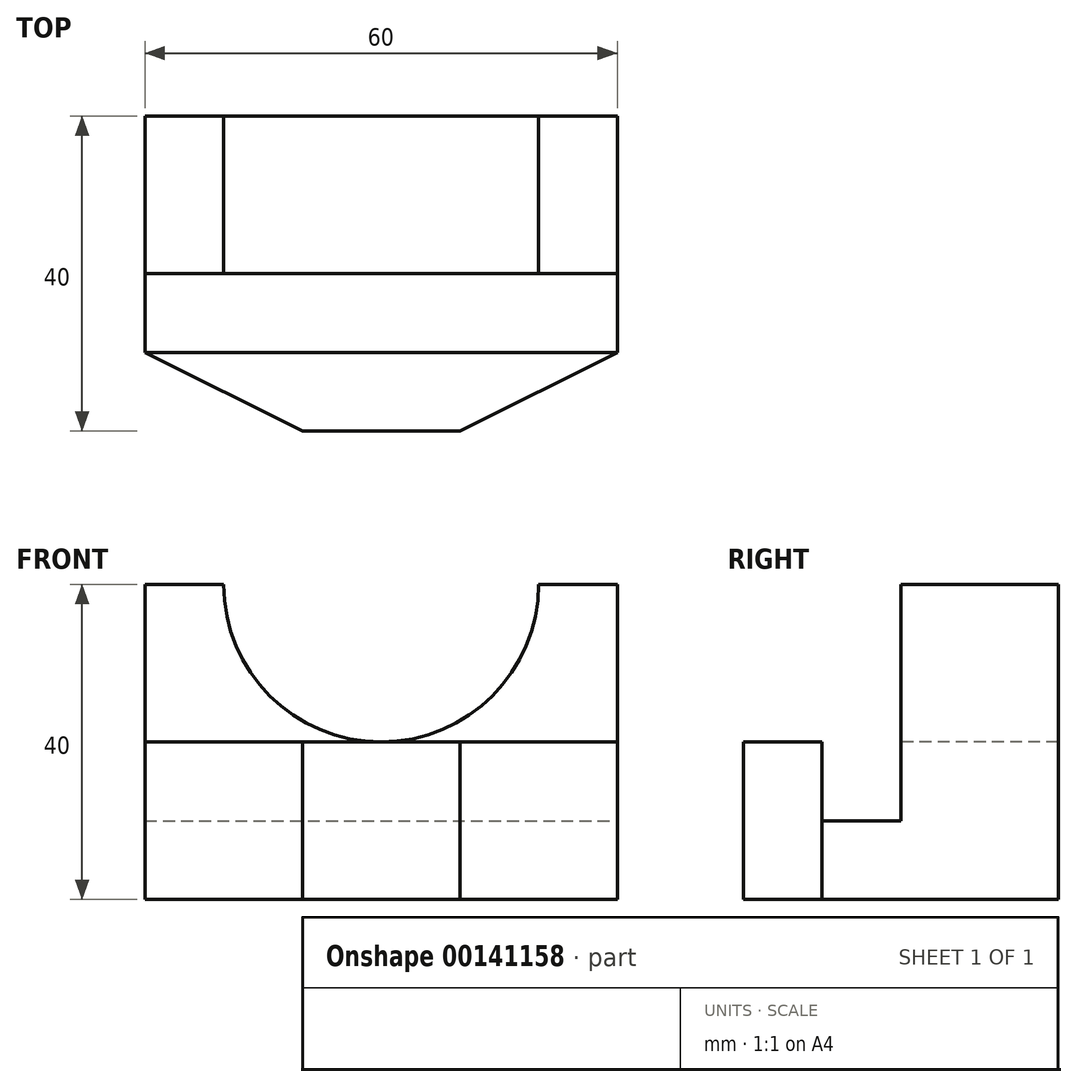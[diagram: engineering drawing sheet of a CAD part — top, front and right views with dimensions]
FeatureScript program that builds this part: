
annotation { "Feature Type Name" : "Feature", "Feature Type Description" : "" }
export const myFeature = defineFeature(function(context is Context, id is Id, definition is map)
    precondition{}
    {
        {
            var Q0;
            Q0=qCreatedBy(makeId("Top.planeOp"),FACE);
            var sketch = newSketch(context, id + "F0", { "sketchPlane" : qUnion([Q0])});
            skLineSegment(sketch, "E0.bottom", {"start": v(20, 0) * mm, "end": v(40, 0) * mm});
            skLineSegment(sketch, "E0.top", {"start": v(0, 40) * mm, "end": v(60, 40) * mm});
            skLineSegment(sketch, "E0.left", {"start": v(0, 10) * mm, "end": v(0, 40) * mm});
            skLineSegment(sketch, "E0.right", {"start": v(60, 10) * mm, "end": v(60, 40) * mm});
            skLineSegment(sketch, "E1", {"start": v(0, 10) * mm, "end": v(20, 0) * mm});
            skLineSegment(sketch, "E2", {"start": v(60, 10) * mm, "end": v(40, 0) * mm});
            skLineSegment(sketch, "E3", {"start": v(0, 10) * mm, "end": v(60, 10) * mm});
            skLineSegment(sketch, "E4", {"start": v(0, 20) * mm, "end": v(60, 20) * mm});
            skLineSegment(sketch, "E5", {"start": v(10, 40) * mm, "end": v(10, 20) * mm});
            skLineSegment(sketch, "E6", {"start": v(50, 20) * mm, "end": v(50, 40) * mm});
            skSolve(sketch);
        }
        {
            var Q0;
            {var subQ3=sQuery(id+"F0.wireOp",EDGE,"E5");Q0=makeQuery(id+"F0.imprint","IMPRINT",FACE,{"disambiguationData":[TD([[makeQuery(id+"F0.imprint","IMPRINT",EDGE,{"derivedFrom":subQ3}),-1.0]])]});}
            var Q1;
            {var subQ0=sQuery(id+"F0.wireOp",EDGE,"E5");Q1=makeQuery(id+"F0.imprint","IMPRINT",FACE,{"disambiguationData":[TD([[makeQuery(id+"F0.imprint","IMPRINT",EDGE,{"derivedFrom":subQ0}),1.0]])]});}
            var Q2;
            {var subQ3=sQuery(id+"F0.wireOp",EDGE,"E6");Q2=makeQuery(id+"F0.imprint","IMPRINT",FACE,{"disambiguationData":[TD([[makeQuery(id+"F0.imprint","IMPRINT",EDGE,{"derivedFrom":subQ3}),-1.0]])]});}
            extrude(context, id + "F1", {"entities" : qUnion([Q0, Q1, Q2]), "depth" : 40 * mm});
        }
        {
            var Q0;
            {var subQ4=sQuery(id+"F0.wireOp",EDGE,"E3");Q0=makeQuery(id+"F0.imprint","IMPRINT",FACE,{"disambiguationData":[TD([[makeQuery(id+"F0.imprint","IMPRINT",EDGE,{"derivedFrom":subQ4}),1.0]])]});}
            extrude(context, id + "F2", {"entities" : qUnion([Q0]), "operationType" : NewBodyOperationType.ADD, "depth" : 10 * mm});
        }
        {
            var Q0;
            Q0=makeQuery(id+"F0.imprint","IMPRINT",FACE,{"disambiguationData":[TD([[makeQuery(id+"F0.imprint","IMPRINT",EDGE,{"derivedFrom":sQuery(id+"F0.wireOp",EDGE,"E0.bottom")}),1.0]])]});
            extrude(context, id + "F3", {"entities" : qUnion([Q0]), "operationType" : NewBodyOperationType.ADD, "depth" : 20 * mm});
        }
        {
            var Q0;
            Q0=makeQuery(id+"F1.opExtrude","SWEPT_FACE",FACE,{"disambiguationData":[OSD([sQuery(id+"F0.wireOp",EDGE,"E4")])]});
            var sketch = newSketch(context, id + "F4", { "sketchPlane" : qUnion([Q0])});
            skLineSegment(sketch, "E7.bottom", {"start": v(0, 40) * mm, "end": v(60, 40) * mm});
            skLineSegment(sketch, "E7.top", {"start": v(0, 20) * mm, "end": v(60, 20) * mm});
            skLineSegment(sketch, "E7.left", {"start": v(0, 40) * mm, "end": v(0, 20) * mm});
            skLineSegment(sketch, "E7.right", {"start": v(60, 40) * mm, "end": v(60, 20) * mm});
            skArc(sketch, "E8", {"start": v(10, 40) * mm, "mid": v(30, 20) * mm, "end": v(50, 40) * mm});
            skSolve(sketch);
        }
        {
            var Q0;
            {var subQ0=sQuery(id+"F4.wireOp",EDGE,"E8");var subQ1=sQuery(id+"F4.wireOp",EDGE,"E7.bottom");var subQ2=makeQuery(id+"F4.imprint","INTERSECT",VERTEX,{"disambiguationData":[OD(0.0)],"derivedFrom":[subQ1,subQ0]});Q0=makeQuery(id+"F4.imprint","IMPRINT",FACE,{"disambiguationData":[TD([[makeQuery(id+"F4.imprint","IMPRINT",EDGE,{"disambiguationData":[TD([[subQ2,-1.0]])],"derivedFrom":subQ1}),-1.0]])]});}
            extrude(context, id + "F5", {"entities" : qUnion([Q0]), "operationType" : NewBodyOperationType.REMOVE, "oppositeDirection" : true, "depth" : 20 * mm});
        }
    });
